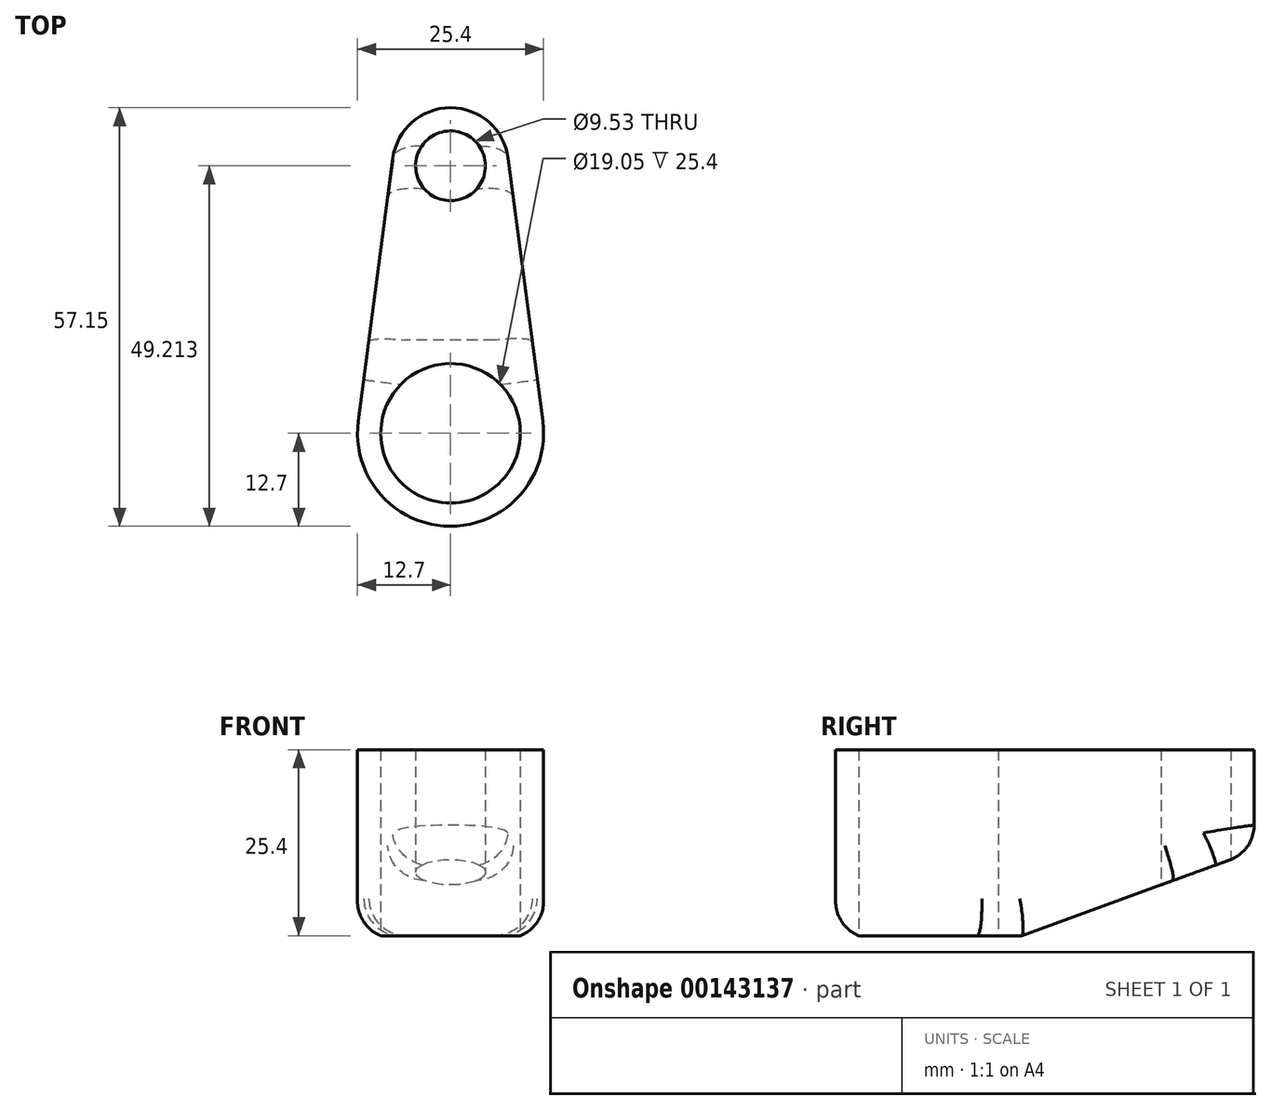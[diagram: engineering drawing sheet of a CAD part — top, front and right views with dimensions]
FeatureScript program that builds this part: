
annotation { "Feature Type Name" : "Feature", "Feature Type Description" : "" }
export const myFeature = defineFeature(function(context is Context, id is Id, definition is map)
    precondition{}
    {
        {
            var Q0;
            Q0=qCreatedBy(makeId("Top.planeOp"),FACE);
            var sketch = newSketch(context, id + "F0", { "sketchPlane" : qUnion([Q0])});
            skCircle(sketch, "E0", {"center": v(0, 0) * mm, "radius": 9.53 * mm});
            skCircle(sketch, "E1", {"center": v(0, 0) * mm, "radius": 12.7 * mm});
            skCircle(sketch, "E2", {"center": v(0, 36.51) * mm, "radius": 7.94 * mm});
            skCircle(sketch, "E3", {"center": v(0, 36.51) * mm, "radius": 4.76 * mm});
            skLineSegment(sketch, "E4", {"start": v(-7.87, 37.55) * mm, "end": v(-12.6, 1.66) * mm});
            skLineSegment(sketch, "E5", {"start": v(7.87, 37.55) * mm, "end": v(12.6, 1.66) * mm});
            skSolve(sketch);
        }
        {
            var Q0;
            Q0=makeQuery(id+"F0.imprint","IMPRINT",FACE,{"disambiguationData":[TD([[makeQuery(id+"F0.imprint","IMPRINT",EDGE,{"derivedFrom":sQuery(id+"F0.wireOp",EDGE,"E3")}),-1.0]])]});
            var Q1;
            Q1=makeQuery(id+"F0.imprint","IMPRINT",FACE,{"disambiguationData":[TD([[makeQuery(id+"F0.imprint","IMPRINT",EDGE,{"derivedFrom":sQuery(id+"F0.wireOp",EDGE,"E0")}),-1.0]])]});
            var Q2;
            {var subQ0=sQuery(id+"F0.wireOp",EDGE,"E4");Q2=makeQuery(id+"F0.imprint","IMPRINT",FACE,{"disambiguationData":[TD([[makeQuery(id+"F0.imprint","IMPRINT",EDGE,{"derivedFrom":subQ0}),1.0]])]});}
            extrude(context, id + "F1", {"entities" : qUnion([Q0, Q1, Q2]), "depth" : 25.4 * mm});
        }
        {
            var Q0;
            Q0=qCreatedBy(makeId("Right.planeOp"),FACE);
            var sketch = newSketch(context, id + "F2", { "sketchPlane" : qUnion([Q0])});
            skLineSegment(sketch, "E6", {"start": v(12.7, 0) * mm, "end": v(48.8, 0) * mm});
            skLineSegment(sketch, "E7", {"start": v(48.8, 0) * mm, "end": v(48.8, 13.14) * mm});
            skLineSegment(sketch, "E8", {"start": v(48.8, 13.14) * mm, "end": v(12.7, 0) * mm});
            skSolve(sketch);
        }
        {
            var Q0;
            Q0 = qSketchRegion(id + "F2", true);
            extrude(context, id + "F3", {"entities" : qUnion([Q0]), "operationType" : NewBodyOperationType.REMOVE, "endBound" : BoundingType.THROUGH_ALL, "depth" : 25.4 * mm, "hasSecondDirection" : true, "secondDirectionBound" : SecondDirectionBoundingType.THROUGH_ALL, "secondDirectionOppositeDirection" : true, "secondDirectionDepth" : 25.4 * mm});
        }
        {
            var Q0;
            Q0=makeQuery(id+"F1.opExtrude","CAP_EDGE",EDGE,{"disambiguationData":[OSD([sQuery(id+"F0.wireOp",EDGE,"E1")])],"isStart":true});
            var Q1;
            Q1=makeQuery(id+"F1.opExtrude","CAP_EDGE",EDGE,{"disambiguationData":[OSD([sQuery(id+"F0.wireOp",EDGE,"E4")])],"isStart":true});
            var Q2;
            Q2=makeQuery(id+"F1.opExtrude","CAP_EDGE",EDGE,{"disambiguationData":[OSD([sQuery(id+"F0.wireOp",EDGE,"E5")])],"isStart":true});
            var Q3;
            Q3=makeQuery(id+"F3.boolean.opBoolean","INTERSECT",EDGE,{"derivedFrom":[makeQuery(id+"F1.opExtrude","SWEPT_FACE",FACE,{"disambiguationData":[OSD([sQuery(id+"F0.wireOp",EDGE,"E4")])]}),makeQuery(id+"F3.opExtrude","SWEPT_FACE",FACE,{"disambiguationData":[OSD([sQuery(id+"F2.wireOp",EDGE,"E8")])]})]});
            var Q4;
            Q4=makeQuery(id+"F3.boolean.opBoolean","INTERSECT",EDGE,{"derivedFrom":[makeQuery(id+"F1.opExtrude","SWEPT_FACE",FACE,{"disambiguationData":[OSD([sQuery(id+"F0.wireOp",EDGE,"E2")])]}),makeQuery(id+"F3.opExtrude","SWEPT_FACE",FACE,{"disambiguationData":[OSD([sQuery(id+"F2.wireOp",EDGE,"E8")])]})]});
            var Q5;
            Q5=makeQuery(id+"F3.boolean.opBoolean","INTERSECT",EDGE,{"derivedFrom":[makeQuery(id+"F1.opExtrude","SWEPT_FACE",FACE,{"disambiguationData":[OSD([sQuery(id+"F0.wireOp",EDGE,"E5")])]}),makeQuery(id+"F3.opExtrude","SWEPT_FACE",FACE,{"disambiguationData":[OSD([sQuery(id+"F2.wireOp",EDGE,"E8")])]})]});
            fillet(context, id + "F4", {"entities" : qUnion([Q0, Q1, Q2, Q3, Q4, Q5]), "radius" : 5.08 * mm, "tangentPropagation" : true, "allowEdgeOverflow" : false});
        }
    });
